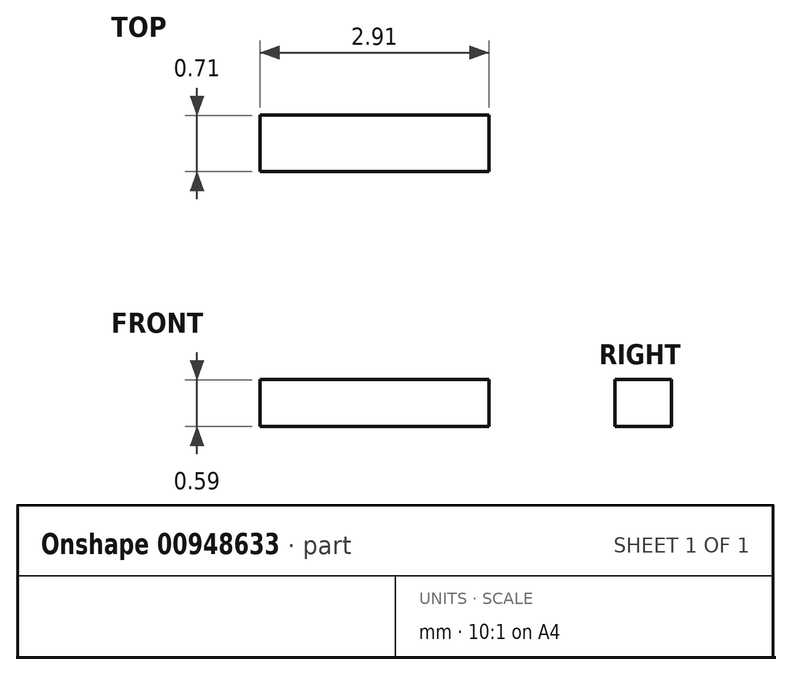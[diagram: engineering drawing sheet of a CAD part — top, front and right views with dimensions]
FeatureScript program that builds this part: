
annotation { "Feature Type Name" : "Feature", "Feature Type Description" : "" }
export const myFeature = defineFeature(function(context is Context, id is Id, definition is map)
    precondition{}
    {
        {
            var Q0;
            Q0=qCreatedBy(makeId("Front.planeOp"),FACE);
            var sketch = newSketch(context, id + "F0", { "sketchPlane" : qUnion([Q0])});
            skLineSegment(sketch, "E0.bottom", {"start": v(0, 0) * mm, "end": v(2.9, 0) * mm});
            skLineSegment(sketch, "E0.top", {"start": v(0, 0.6) * mm, "end": v(2.9, 0.6) * mm});
            skLineSegment(sketch, "E0.left", {"start": v(0, 0) * mm, "end": v(0, 0.6) * mm});
            skLineSegment(sketch, "E0.right", {"start": v(2.9, 0) * mm, "end": v(2.9, 0.6) * mm});
            skSolve(sketch);
        }
        {
            var Q0;
            Q0=makeQuery(id+"F0.imprint","IMPRINT",FACE,{"disambiguationData":[TD([[makeQuery(id+"F0.imprint","IMPRINT",EDGE,{"derivedFrom":sQuery(id+"F0.wireOp",EDGE,"E0.bottom")}),1.0]])]});
            extrude(context, id + "F1", {"entities" : qUnion([Q0]), "oppositeDirection" : true, "depth" : 0.71 * mm, "offsetDistance" : 25.4 * mm});
        }
    });
